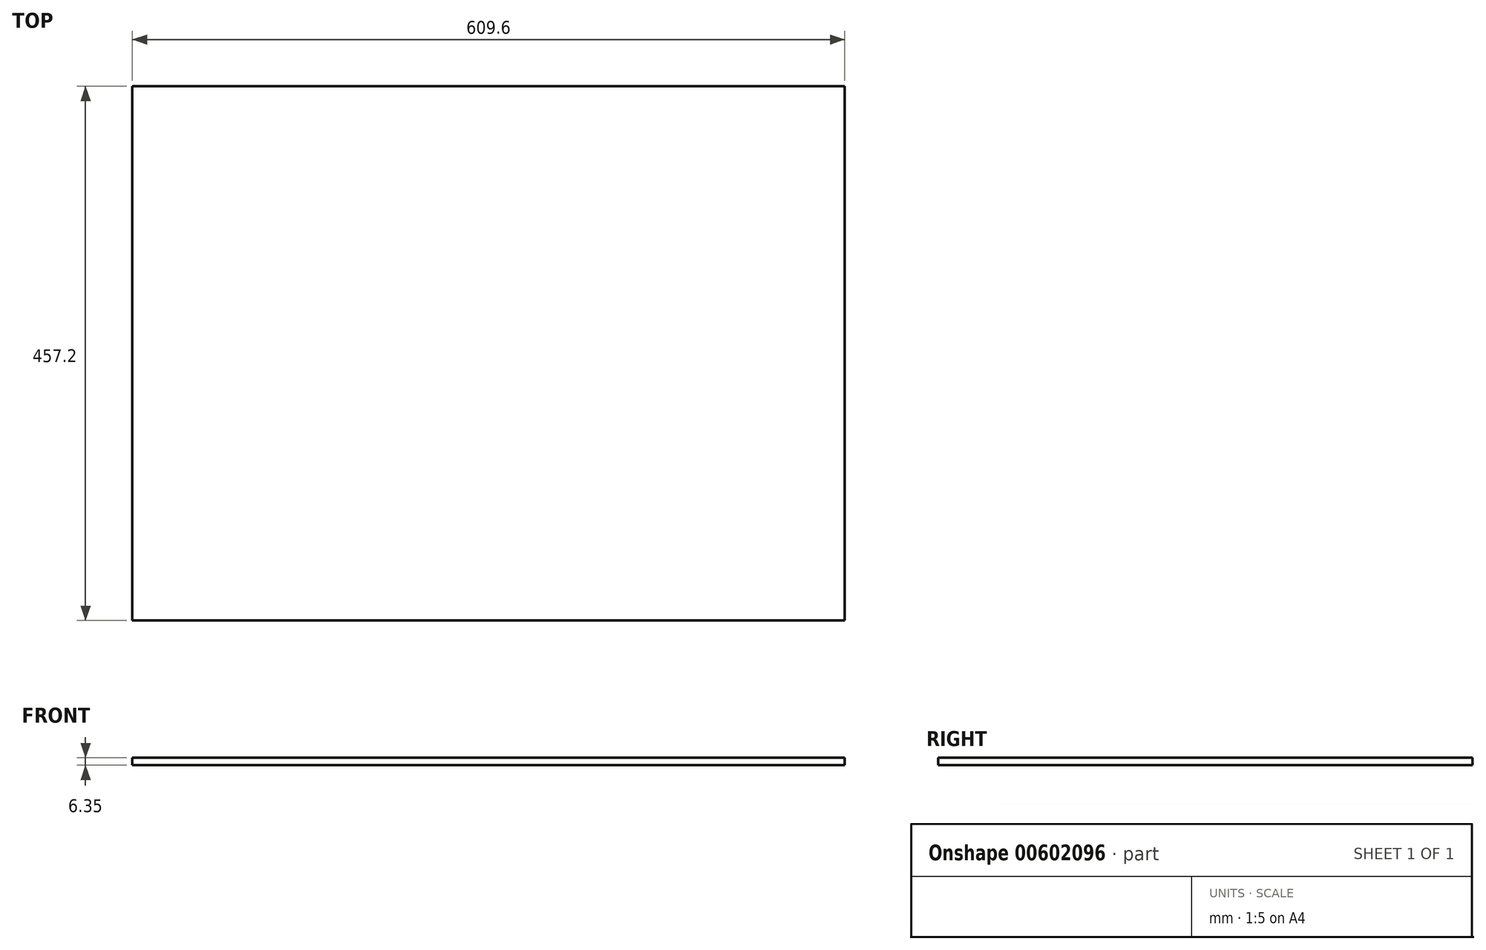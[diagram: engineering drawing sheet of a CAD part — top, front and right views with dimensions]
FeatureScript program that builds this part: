
annotation { "Feature Type Name" : "Feature", "Feature Type Description" : "" }
export const myFeature = defineFeature(function(context is Context, id is Id, definition is map)
    precondition{}
    {
        {
            var Q0;
            Q0=qCreatedBy(makeId("Top.planeOp"),FACE);
            var sketch = newSketch(context, id + "F0", { "sketchPlane" : qUnion([Q0])});
            skLineSegment(sketch, "E0.bottom", {"start": v(304.8, 228.6) * mm, "end": v(-304.8, 228.6) * mm});
            skLineSegment(sketch, "E0.top", {"start": v(304.8, -228.6) * mm, "end": v(-304.8, -228.6) * mm});
            skLineSegment(sketch, "E0.left", {"start": v(304.8, 228.6) * mm, "end": v(304.8, -228.6) * mm});
            skLineSegment(sketch, "E0.right", {"start": v(-304.8, 228.6) * mm, "end": v(-304.8, -228.6) * mm});
            skPoint(sketch, "E0.middle", {"position": v(0, 0) * mm});
            skSolve(sketch);
        }
        {
            var Q0;
            Q0=makeQuery(id+"F0.imprint","IMPRINT",FACE,{"disambiguationData":[TD([[makeQuery(id+"F0.imprint","IMPRINT",EDGE,{"derivedFrom":sQuery(id+"F0.wireOp",EDGE,"E0.bottom")}),1.0]])]});
            extrude(context, id + "F1", {"entities" : qUnion([Q0]), "depth" : 6.35 * mm, "offsetDistance" : 25.4 * mm});
        }
    });
